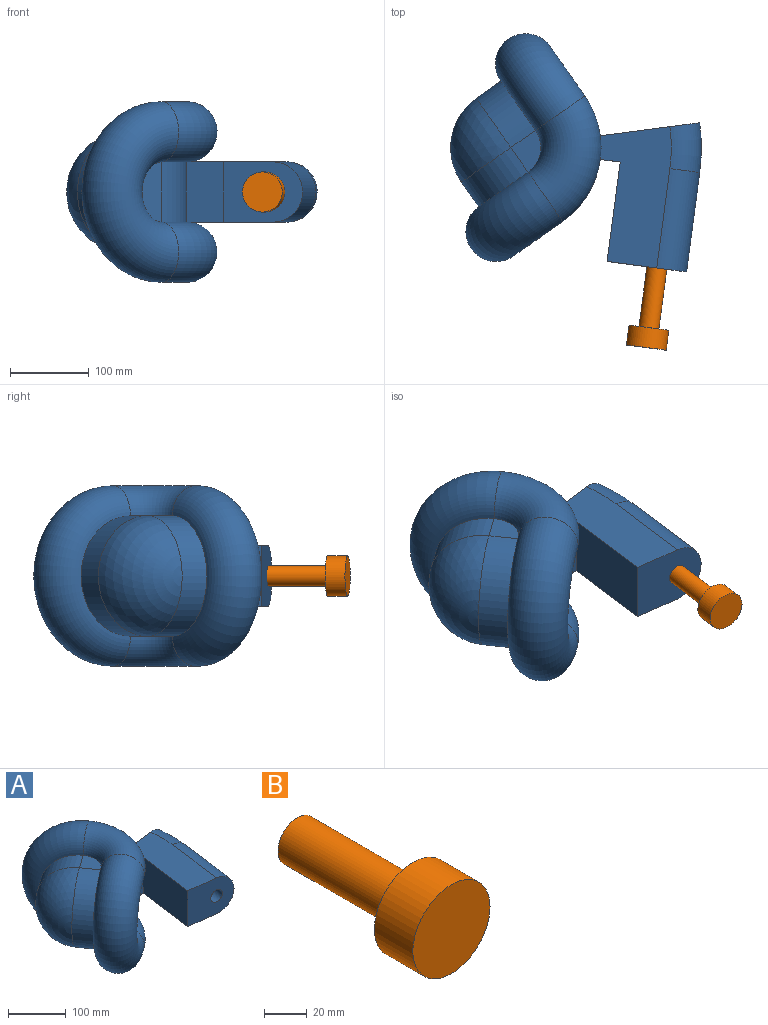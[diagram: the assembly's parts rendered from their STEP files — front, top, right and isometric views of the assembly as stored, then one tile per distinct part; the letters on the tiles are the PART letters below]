
ASSEMBLY  parts=2 mates=1
PART A: 27 faces, bbox 319.6x302.5x247.4 mm
  f0: plane 76.2x62.96mm, normal (-0.13,-0.99,0), area 4838.7mm2, adj f2,f14,f17,f19
  f1: cylinder r=76.2mm len=76.2mm, axis (0,0,1), area 2786.9mm2, adj f3,f11,f12,f18
  f2: cylinder r=76.2mm len=76.2mm, axis (0,0,1), area 4813.7mm2, adj f0,f3,f5,f12
  f3: torus R=76.2mm, axis (0,0,1), area 23770.4mm2, adj f1,f2,f4,f6,f10,f17
  f4: plane 53.06x38.1mm, normal (0,0,1), area 1140.1mm2, adj f3,f7,f9
  f5: plane 76.2x31.21mm, normal (0.57,-0.82,0), area 2280.2mm2, adj f2,f6
  f6: torus R=76.2mm, axis (-0.57,0.82,0), area 47540.8mm2, adj f3,f5,f7,f12
  f7: cylinder r=76.2mm len=152.4mm, axis (-0.57,0.82,0), area 9120.7mm2, adj f4,f6,f8,f13
  f8: sphere r=76.2mm, area 18241.5mm2, adj f7,f9
  f9: cylinder r=76.2mm len=152.4mm, axis (0.82,0.57,0), area 9120.7mm2, adj f4,f8,f10,f13
  f10: torus R=76.2mm, axis (0.82,0.57,0), area 47540.8mm2, adj f3,f9,f11,f12
  f11: plane 76.2x31.21mm, normal (0.82,0.57,0), area 2280.2mm2, adj f1,f10
  f12: torus R=76.2mm, axis (0,0,-1), area 23770.4mm2, adj f1,f2,f6,f10,f13,f14
  f13: plane 53.06x38.1mm, normal (0,0,-1), area 1140.1mm2, adj f7,f9,f12
  f14: plane 178.96x127.65mm, normal (0,0,-1), area 12709.3mm2, adj f0,f12,f15,f18,f19,f21,f22
  f15: torus R=203.2mm, axis (0,0,-1), area 7127.5mm2, adj f14,f17,f18,f21
  f16: torus R=203.2mm, axis (0,0,-1), area 4245mm2, adj f18,f20
  f17: plane 178.96x127.65mm, normal (0,0,1), area 12709.3mm2, adj f0,f3,f15,f18,f19,f21,f22
  f18: plane 163.69x76.2mm, normal (-0.13,0.99,0), area 11450.9mm2, adj f1,f14,f15,f16,f17
  f19: plane 125.91x76.2mm, normal (-0.99,0.13,0), area 9677.4mm2, adj f0,f14,f17,f22
  f20: cylinder r=12.7mm len=129.23mm, axis (0.13,0.99,0), area 10134.1mm2, adj f16,f22
  f21: cylinder r=38.1mm len=130.89mm, axis (0.13,0.99,0), area 15201.2mm2, adj f14,f15,f17,f22
  f22: plane 100.73x76.2mm, normal (-0.13,-0.99,0), area 6612.2mm2, adj f14,f17,f19,f20,f21
  f23: torus R=76.2mm, axis (0,0,1), area 14326.8mm2, adj f24,f26
  f24: torus R=76.2mm, axis (-0.57,0.82,0), area 28653.6mm2, adj f23,f25
  f25: torus R=76.2mm, axis (0,0,-1), area 14326.8mm2, adj f24,f26
  f26: torus R=76.2mm, axis (0.82,0.57,0), area 28653.6mm2, adj f23,f25
PART B: 5 faces, bbox 50.8x101.6x50.8 mm
  f0: cylinder r=12.7mm len=76.2mm, axis (0,1,0), area 6080.5mm2, adj f1,f4
  f1: plane 25.4x25.4mm, normal (0,1,0), area 506.7mm2, adj f0
  f2: cylinder r=25.4mm len=50.8mm, axis (0,1,0), area 4053.7mm2, adj f3,f4
  f3: plane 50.8x50.8mm, normal (0,-1,0), area 2026.8mm2, adj f2
  f4: plane 50.8x50.8mm, normal (0,1,0), area 1520.1mm2, adj f0,f2
PLACE A at identity fixed
PLACE B rot(axis=(0,0,-1),7.5deg) t=(146.78,-152.44,-38.1)mm
MATE slider B.f0 <-> A.f20  axis (0.13,0.99,0) through (146.78,-152.44,-38.1)mm
